# Revit family: FantiniCosmi_BIM_C800WIFIR
name_source: partatom
category: Generic Models
units: mm (PartAtom-declared; Revit-internal decimal feet)

## family parameters
Always vertical = Yes
Can host rebar = No
Cut with Voids When Loaded = No
Part Type = Normal
Room Calculation Point = No
Round Connector Dimension = Use Diameter
Shared = No
Work Plane-Based = No

## types (1)
- Standard
    Ambient RH display range = 0 ÷ 99 %, increase 1%
    Catalog web link = https://www.fantinicosmi.it
    Default Elevation = 0 mm  [stored 0 ft]
    Description = Led Programmable Thermostat with Smart functions, batteries power supplied
    Designer = Carniti
    Differential = 0.3 ÷ 5 K
    Maximum absorbed power = 5 W
    Maximum radio frequency power transmitted = <10mW
    Maximum room temperature = 45°C
    Measurement scale/room T display = – 50 ÷ + 50 °C
    Output type = 1 relay for heating and cooling systems (3 screw clamps (closed + open)
    Part Number = C800WIFIR
    Pollution degree = 2
    Power supply = 2 batteries 1,5V AA or 3,3 Vdc @1500mA Max (by C800AL)
    Protection degree = IP30
    Pulse voltage = 4000V
    Router communication port = 1080
    Software Class = A
    Storage temperature = -10°C ÷ +60°C
    Temperature regulation scale = 2 ÷ 40 °C, increment 0.1°C
    Thermal gradient = 4 K/h
    Type of action = 1 B.U. (connection micro-switch)
    WiFi connection = 2.4 GHz (802.11 b/g/n)

note: [stored X ft] marks values corroborated as IEEE doubles in the binary element streams (Revit-internal decimal feet)

## geometry (parser evidence)
native form markers: Sweep x3
no freeform markers — native parametric forms only
